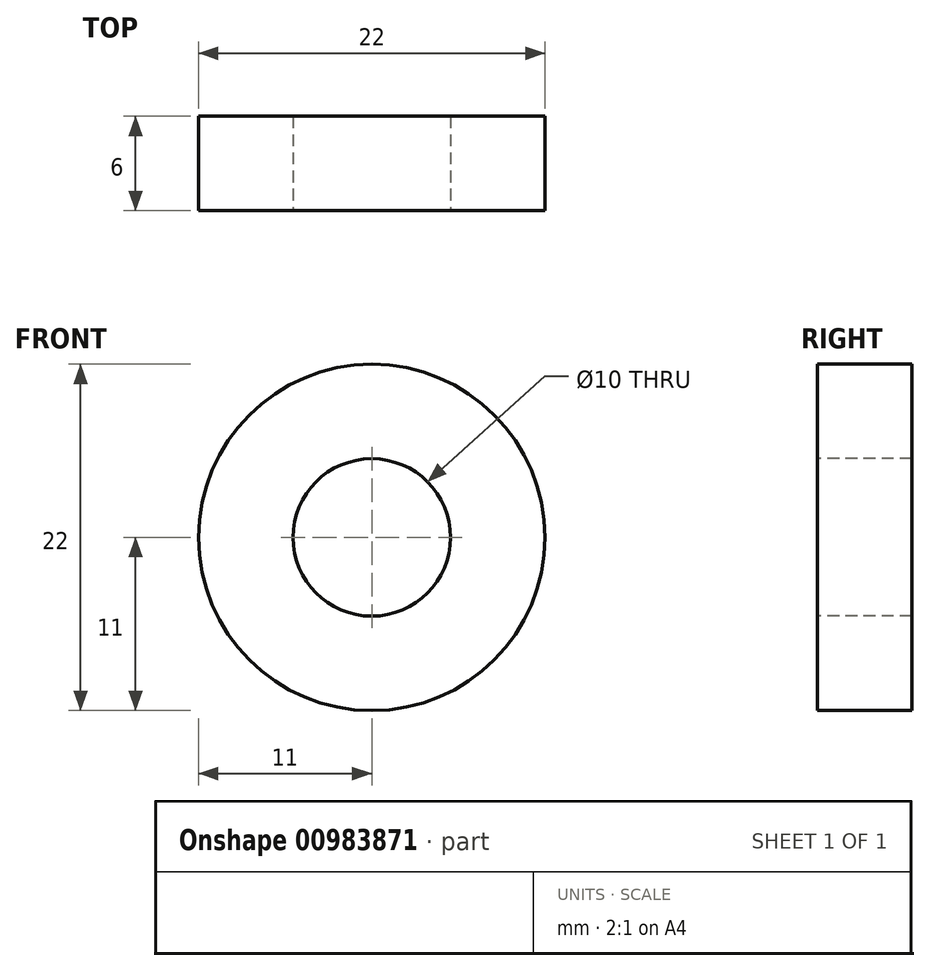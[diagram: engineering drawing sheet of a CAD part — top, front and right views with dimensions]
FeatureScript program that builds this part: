
annotation { "Feature Type Name" : "Feature", "Feature Type Description" : "" }
export const myFeature = defineFeature(function(context is Context, id is Id, definition is map)
    precondition{}
    {
        {
            var Q0;
            Q0=qCreatedBy(makeId("Front.planeOp"),FACE);
            var sketch = newSketch(context, id + "F0", { "sketchPlane" : qUnion([Q0])});
            skCircle(sketch, "E0", {"center": v(0, 0) * mm, "radius": 5 * mm});
            skCircle(sketch, "E1", {"center": v(0, 0) * mm, "radius": 11 * mm});
            skSolve(sketch);
        }
        {
            var Q0;
            Q0=makeQuery(id+"F0.imprint","IMPRINT",FACE,{"disambiguationData":[TD([[makeQuery(id+"F0.imprint","IMPRINT",EDGE,{"derivedFrom":sQuery(id+"F0.wireOp",EDGE,"E0")}),-1.0]])]});
            extrude(context, id + "F1", {"entities" : qUnion([Q0]), "oppositeDirection" : true, "depth" : 6 * mm, "offsetDistance" : 25 * mm});
        }
    });
